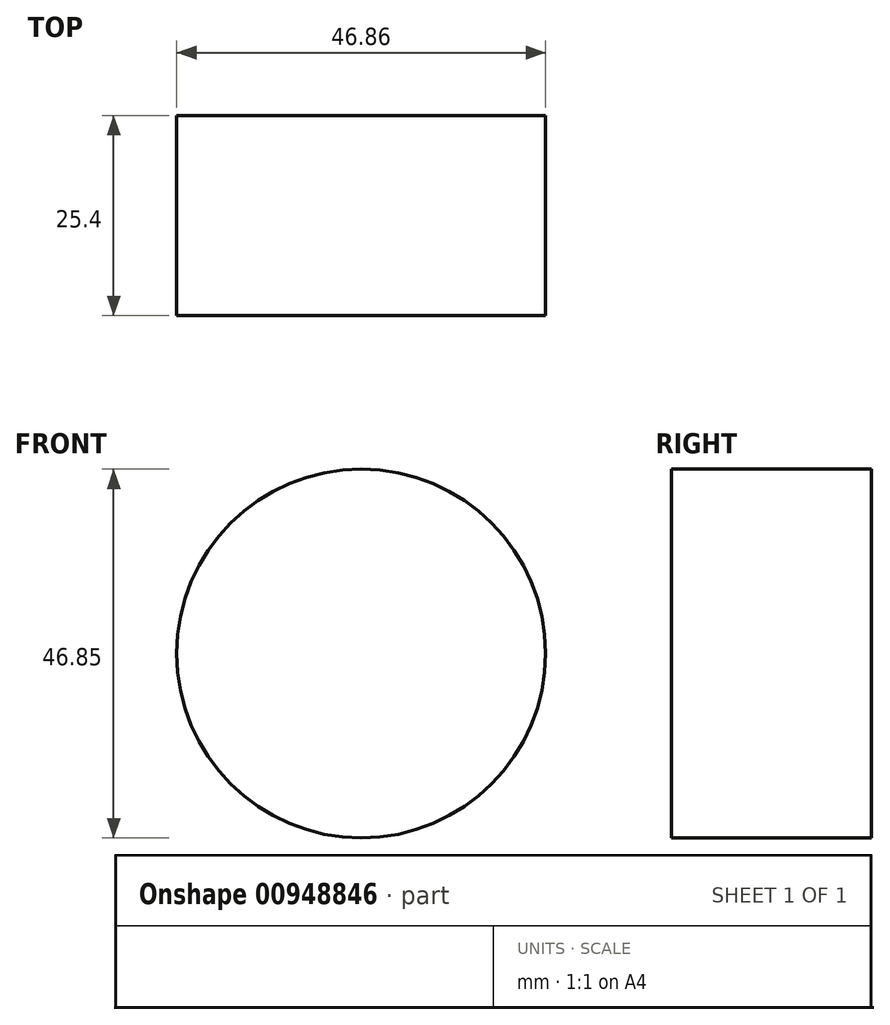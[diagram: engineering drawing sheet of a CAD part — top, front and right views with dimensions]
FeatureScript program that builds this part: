
annotation { "Feature Type Name" : "Feature", "Feature Type Description" : "" }
export const myFeature = defineFeature(function(context is Context, id is Id, definition is map)
    precondition{}
    {
        {
            var Q0;
            Q0=qCreatedBy(makeId("Front.planeOp"),FACE);
            var sketch = newSketch(context, id + "F0", { "sketchPlane" : qUnion([Q0])});
            skCircle(sketch, "E0", {"center": v(-60.59, 19.44) * mm, "radius": 23.43 * mm});
            skSolve(sketch);
        }
        {
            var Q0;
            Q0 = qSketchRegion(id + "F0", true);
            extrude(context, id + "F1", {"entities" : qUnion([Q0]), "depth" : 25.4 * mm, "offsetDistance" : 25.4 * mm});
        }
    });
